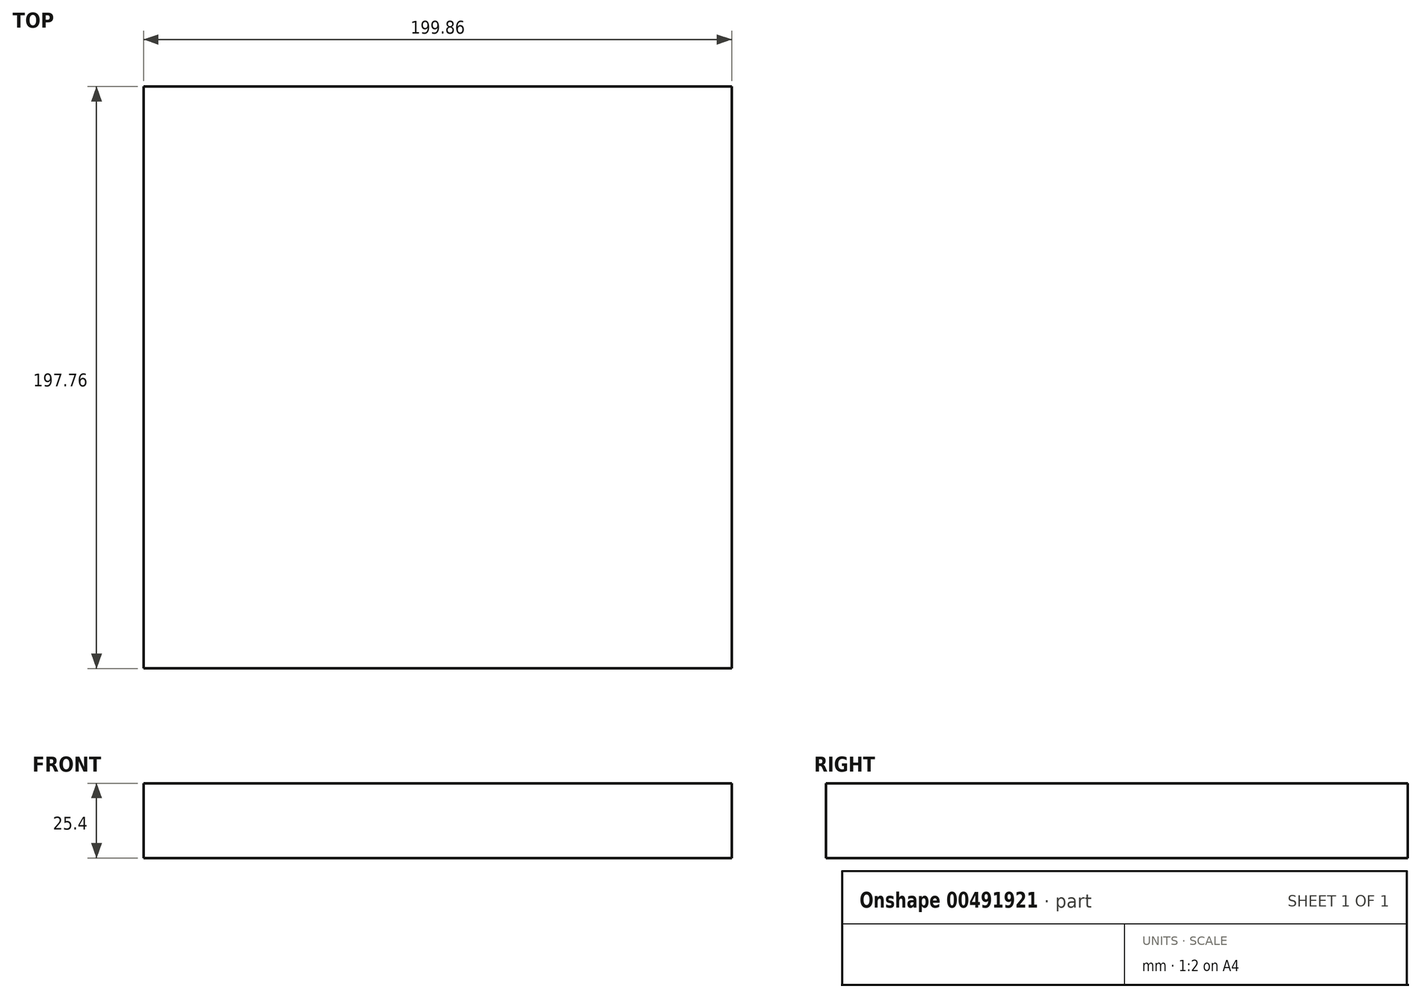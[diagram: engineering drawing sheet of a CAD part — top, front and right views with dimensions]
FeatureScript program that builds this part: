
annotation { "Feature Type Name" : "Feature", "Feature Type Description" : "" }
export const myFeature = defineFeature(function(context is Context, id is Id, definition is map)
    precondition{}
    {
        {
            var Q0;
            Q0=qCreatedBy(makeId("Top.planeOp"),FACE);
            var sketch = newSketch(context, id + "F0", { "sketchPlane" : qUnion([Q0])});
            skLineSegment(sketch, "E0.bottom", {"start": v(99.93, 98.88) * mm, "end": v(-99.93, 98.88) * mm});
            skLineSegment(sketch, "E0.top", {"start": v(99.93, -98.88) * mm, "end": v(-99.93, -98.88) * mm});
            skLineSegment(sketch, "E0.left", {"start": v(99.93, 98.88) * mm, "end": v(99.93, -98.88) * mm});
            skLineSegment(sketch, "E0.right", {"start": v(-99.93, 98.88) * mm, "end": v(-99.93, -98.88) * mm});
            skPoint(sketch, "E0.middle", {"position": v(0, 0) * mm});
            skSolve(sketch);
        }
        {
            var Q0;
            Q0=makeQuery(id+"F0.imprint","IMPRINT",FACE,{"disambiguationData":[TD([[makeQuery(id+"F0.imprint","IMPRINT",EDGE,{"derivedFrom":sQuery(id+"F0.wireOp",EDGE,"E0.bottom")}),1.0]])]});
            extrude(context, id + "F1", {"entities" : qUnion([Q0]), "depth" : 25.4 * mm});
        }
    });
